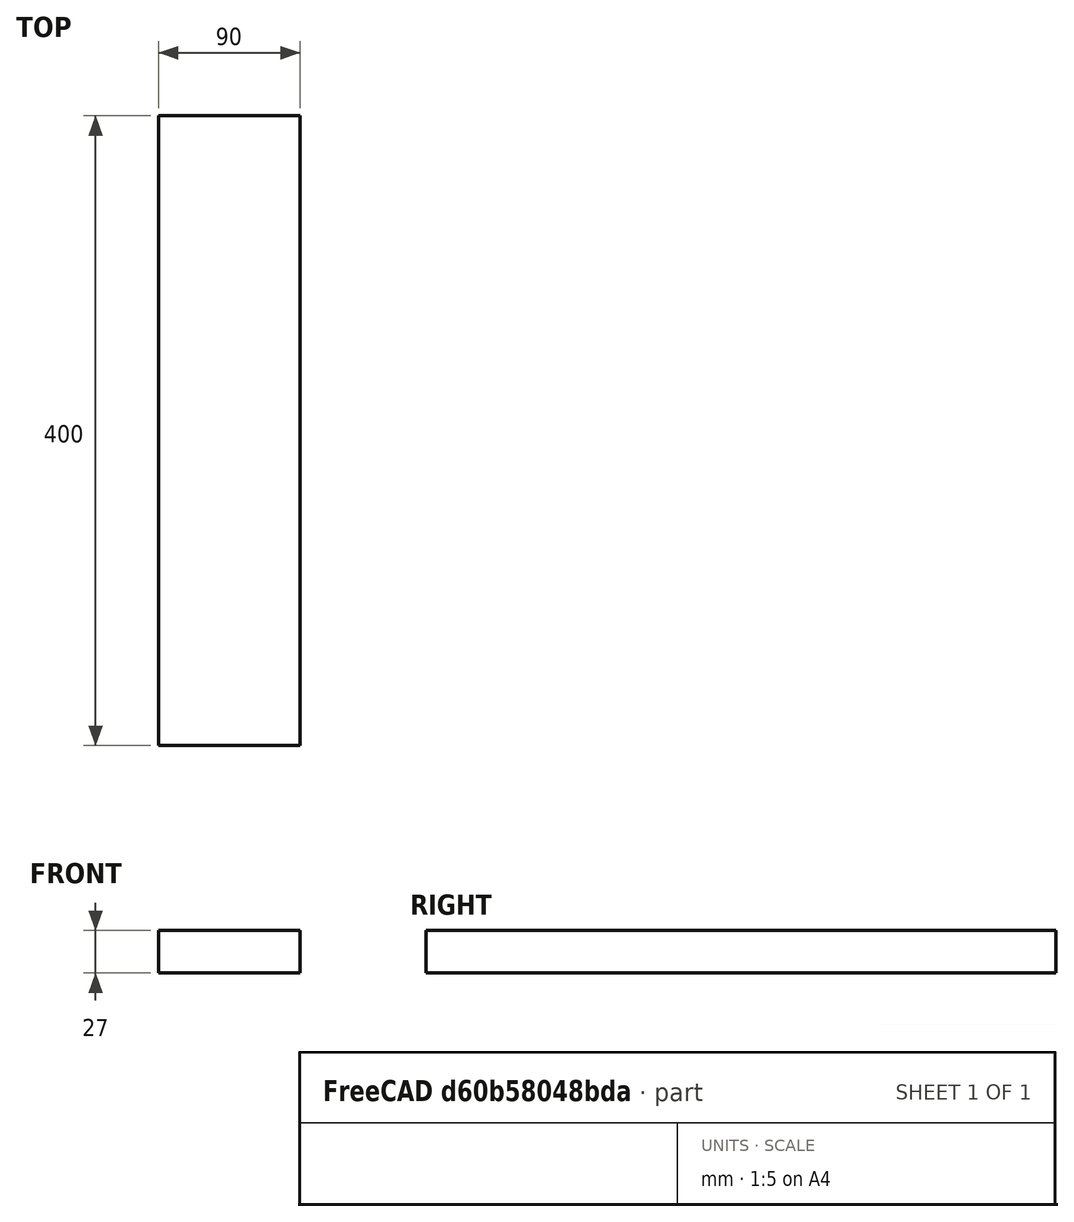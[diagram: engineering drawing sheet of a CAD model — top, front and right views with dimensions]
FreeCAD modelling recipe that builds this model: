
FCSTD DOCUMENT  (FreeCAD 0.20R25131 (Git))
Label: Klemmfläche
License: All rights reserved
LicenseURL: http://en.wikipedia.org/wiki/All_rights_reserved
objects: Part::FeaturePython×7, App::FeaturePython×2, Part::Box×1
note: 7 computed .brp shape members not serialized (recipe doc carries the construction recipe); baked Part::Feature solids carry a one-line shape summary decoded from their .brp
EXTERNAL_REF file=Grunddaten.FCStd obj=Spreadsheet

FEATURE [Part::Box] Box  label="Cube"
  AttacherType = Attacher::AttachEngine3D
  Height = 27
  Length = 90
  Width = 400
  expr: Length = <<Grunddaten>>#Spreadsheet.Klemmflaeche
  expr: Width = <<Grunddaten>>#Spreadsheet.Plattenbreite
  expr: Height = <<Grunddaten>>#Spreadsheet.Plattendicke
FEATURE [App::FeaturePython] Constraints  # WARN: FeaturePython — macro-defined, semantics opaque (R4)
  _Version = 1
FEATURE [Part::FeaturePython] Parts  # WARN: FeaturePython — macro-defined, semantics opaque (R4)
  Group = -> [Box]
  GroupMode = 0
FEATURE [Part::FeaturePython] Assembly  label="Klemmfläche"  # WARN: FeaturePython — macro-defined, semantics opaque (R4)
  AutoRelax = true
  BuildShape = 0
  Freeze = false
  Group = -> [Constraints,Elements,Parts]
  Verbose = false
  _SolverType = 1
  _Version = 1
FEATURE [App::FeaturePython] Elements  # WARN: FeaturePython — macro-defined, semantics opaque (R4)
  Group = -> [Element,Element001,Element002,Element003,Element004]
FEATURE [Part::FeaturePython] Element  label="Vorne"  # link proxy (typed FeaturePython)
  Detach = false
  LinkTransform = true
  LinkedObject = -> Box [Face3]
  _Parent = -> Elements
FEATURE [Part::FeaturePython] Element001  label="Unten"  # link proxy (typed FeaturePython)
  Detach = false
  LinkTransform = true
  LinkedObject = -> Box [Face5]
  _Parent = -> Elements
FEATURE [Part::FeaturePython] Element002  label="Rechts"  # link proxy (typed FeaturePython)
  Detach = false
  LinkTransform = true
  LinkedObject = -> Box [Face2]
  _Parent = -> Elements
FEATURE [Part::FeaturePython] Element003  label="Links"  # link proxy (typed FeaturePython)
  Detach = false
  LinkTransform = true
  LinkedObject = -> Box [Face1]
  _Parent = -> Elements
FEATURE [Part::FeaturePython] Element004  # link proxy (typed FeaturePython)
  Detach = false
  LinkTransform = true
  LinkedObject = -> Box [Face6]
  _Parent = -> Elements
